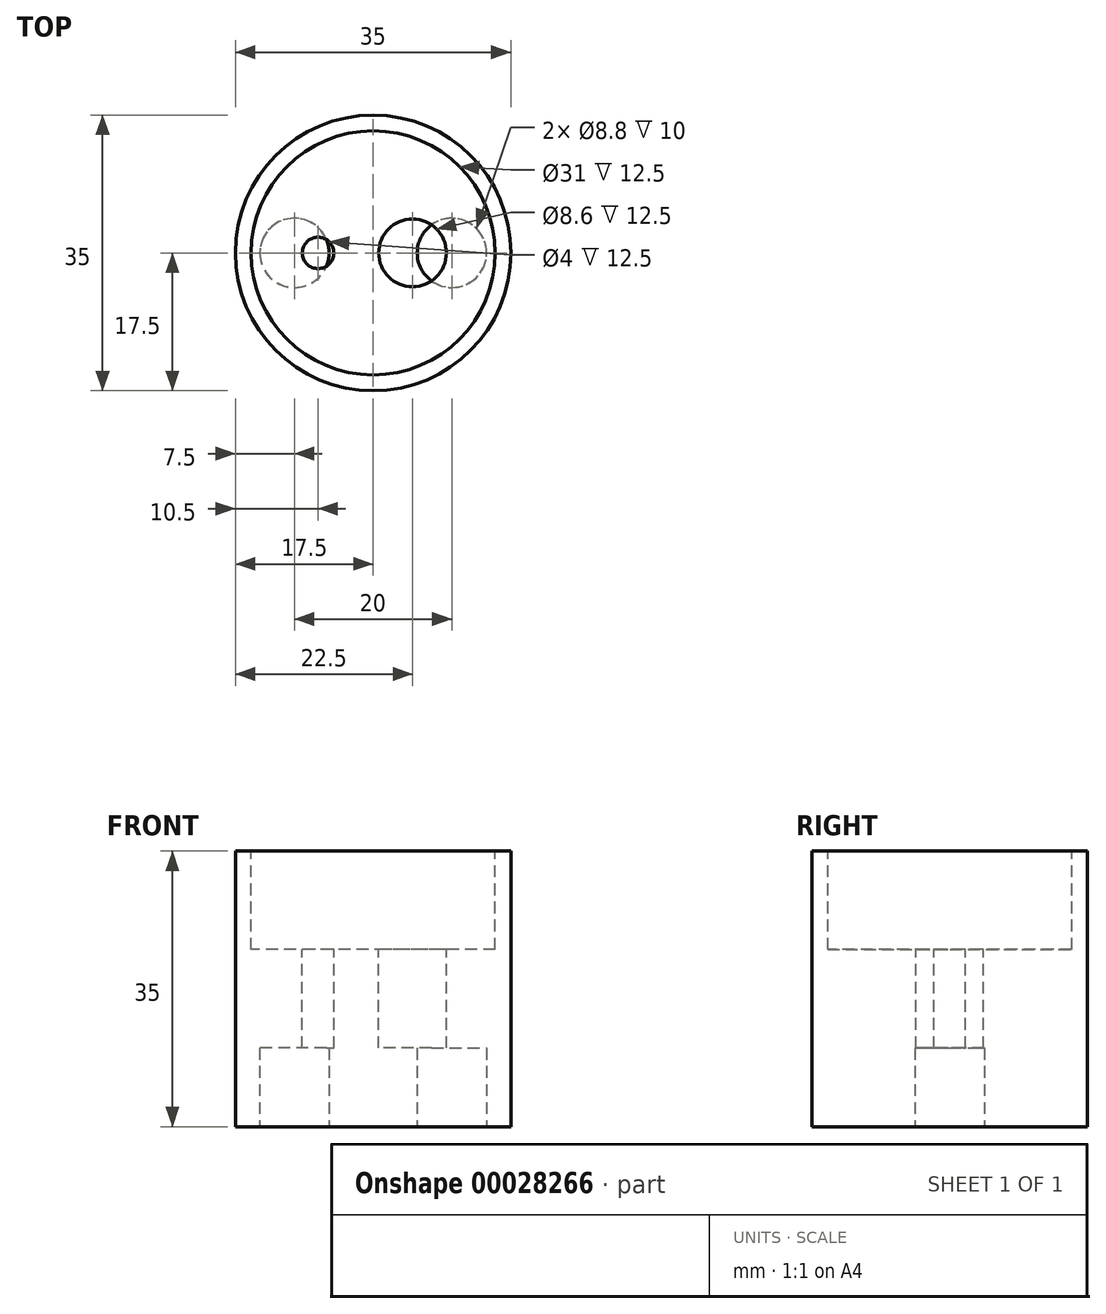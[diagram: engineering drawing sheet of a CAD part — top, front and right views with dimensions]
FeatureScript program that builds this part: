
annotation { "Feature Type Name" : "Feature", "Feature Type Description" : "" }
export const myFeature = defineFeature(function(context is Context, id is Id, definition is map)
    precondition{}
    {
        {
            var Q0;
            Q0=qCreatedBy(makeId("Top.planeOp"),FACE);
            var sketch = newSketch(context, id + "F0", { "sketchPlane" : qUnion([Q0])});
            skCircle(sketch, "E0", {"center": v(0, 0) * mm, "radius": 17.5 * mm});
            skSolve(sketch);
        }
        {
            var Q0;
            Q0=makeQuery(id+"F0.imprint","IMPRINT",FACE,{"disambiguationData":[TD([[makeQuery(id+"F0.imprint","IMPRINT",EDGE,{"derivedFrom":sQuery(id+"F0.wireOp",EDGE,"E0")}),1.0]])]});
            extrude(context, id + "F1", {"entities" : qUnion([Q0]), "depth" : 35 * mm});
        }
        {
            var Q0;
            Q0=makeQuery(id+"F1.opExtrude","CAP_FACE",FACE,{"disambiguationData":[OSD([sQuery(id+"F0.wireOp",EDGE,"E0")])],"isStart":false});
            var sketch = newSketch(context, id + "F2", { "sketchPlane" : qUnion([Q0])});
            skCircle(sketch, "E1", {"center": v(0, 0) * mm, "radius": 15.5 * mm});
            skSolve(sketch);
        }
        {
            var Q0;
            Q0=qSketchRegion(id+"F2",true);
            var Q1;
            Q1=makeQuery(id+"F2.imprint","IMPRINT",FACE,{"disambiguationData":[TD([[makeQuery(id+"F2.imprint","IMPRINT",EDGE,{"derivedFrom":sQuery(id+"F2.wireOp",EDGE,"E1")}),1.0]])]});
            extrude(context, id + "F3", {"entities" : qUnion([Q0, Q1]), "operationType" : NewBodyOperationType.REMOVE, "oppositeDirection" : true, "depth" : 12.5 * mm});
        }
        {
            var Q0;
            Q0=makeQuery(id+"F3.boolean.opBoolean","COPY",FACE,{"derivedFrom":makeQuery(id+"F3.opExtrude","CAP_FACE",FACE,{"disambiguationData":[OSD([sQuery(id+"F2.wireOp",EDGE,"E1")])],"isStart":false})});
            var sketch = newSketch(context, id + "F4", { "sketchPlane" : qUnion([Q0])});
            skCircle(sketch, "E2", {"center": v(0, 0) * mm, "radius": 10 * mm});
            skCircle(sketch, "E3", {"center": v(5, 0) * mm, "radius": 4.3 * mm});
            skCircle(sketch, "E4", {"center": v(-7, 0) * mm, "radius": 2 * mm});
            skSolve(sketch);
        }
        {
            var Q0;
            Q0=makeQuery(id+"F4.imprint","IMPRINT",FACE,{"disambiguationData":[TD([[makeQuery(id+"F4.imprint","IMPRINT",EDGE,{"derivedFrom":sQuery(id+"F4.wireOp",EDGE,"E4")}),1.0]])]});
            var Q1;
            Q1=makeQuery(id+"F4.imprint","IMPRINT",FACE,{"disambiguationData":[TD([[makeQuery(id+"F4.imprint","IMPRINT",EDGE,{"derivedFrom":sQuery(id+"F4.wireOp",EDGE,"E3")}),1.0]])]});
            extrude(context, id + "F5", {"entities" : qUnion([Q0, Q1]), "operationType" : NewBodyOperationType.REMOVE, "oppositeDirection" : true, "depth" : 12.5 * mm});
        }
        {
            var Q0;
            Q0=makeQuery(id+"F1.opExtrude","CAP_FACE",FACE,{"disambiguationData":[OSD([sQuery(id+"F0.wireOp",EDGE,"E0")])],"isStart":true});
            var sketch = newSketch(context, id + "F6", { "sketchPlane" : qUnion([Q0])});
            skCircle(sketch, "E5", {"center": v(0, 0) * mm, "radius": 16 * mm});
            skCircle(sketch, "E6", {"center": v(-10, 0) * mm, "radius": 4.4 * mm});
            skCircle(sketch, "E7", {"center": v(10, 0) * mm, "radius": 4.4 * mm});
            skSolve(sketch);
        }
        {
            var Q0;
            Q0=makeQuery(id+"F6.imprint","IMPRINT",FACE,{"disambiguationData":[TD([[makeQuery(id+"F6.imprint","IMPRINT",EDGE,{"derivedFrom":sQuery(id+"F6.wireOp",EDGE,"E6")}),1.0]])]});
            var Q1;
            Q1=makeQuery(id+"F6.imprint","IMPRINT",FACE,{"disambiguationData":[TD([[makeQuery(id+"F6.imprint","IMPRINT",EDGE,{"derivedFrom":sQuery(id+"F6.wireOp",EDGE,"E7")}),1.0]])]});
            extrude(context, id + "F7", {"entities" : qUnion([Q0, Q1]), "operationType" : NewBodyOperationType.REMOVE, "oppositeDirection" : true, "depth" : 10 * mm});
        }
    });
